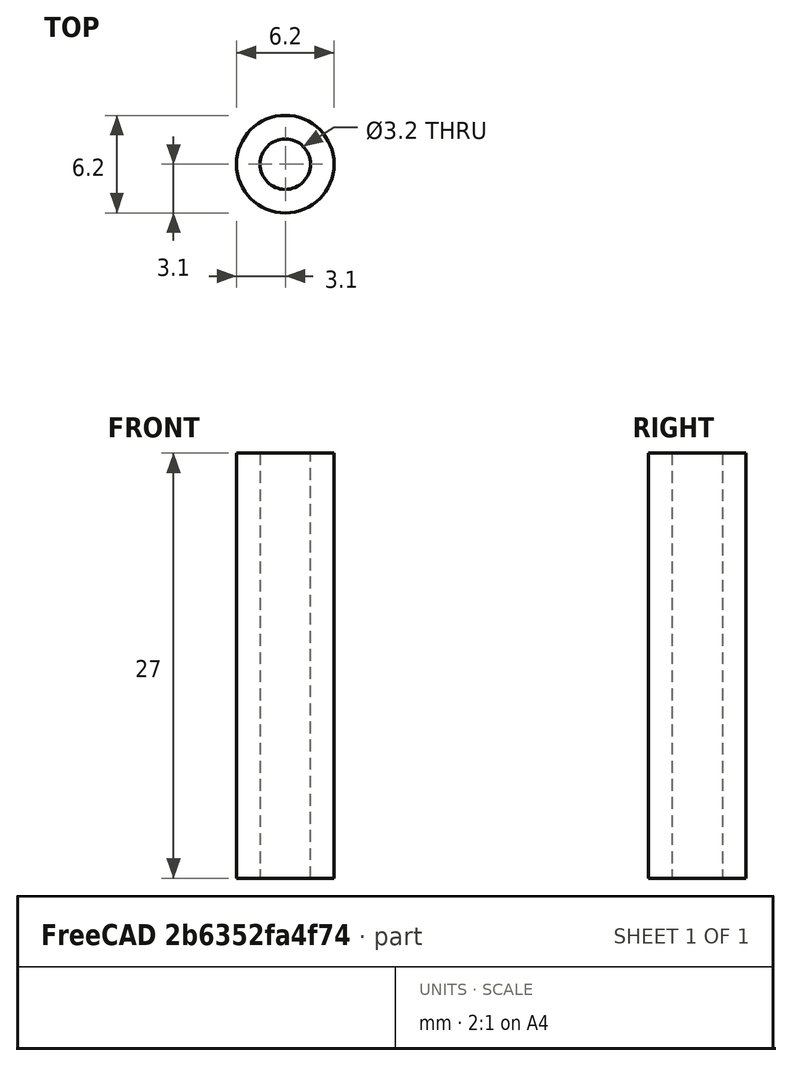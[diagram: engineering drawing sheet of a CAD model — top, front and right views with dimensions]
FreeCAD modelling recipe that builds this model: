
FCSTD DOCUMENT  (FreeCAD 0.20R29603 (Git))
Label: espacador-27mm
License: All rights reserved
LicenseURL: http://en.wikipedia.org/wiki/All_rights_reserved
objects: Sketcher::SketchObject×1, PartDesign::Pad×1, PartDesign::Body×1
note: 4 computed .brp shape members not serialized (recipe doc carries the construction recipe); baked Part::Feature solids carry a one-line shape summary decoded from their .brp

FEATURE [Sketcher::SketchObject] Sketch
  FullyConstrained = true
  MapMode = 5
  Support = -> [XY_Plane]
  sketch-geometry (4):
    g0: Circle CenterX=0 CenterY=0 CenterZ=0 NormalX=0 NormalY=0 NormalZ=1 AngleXU=0 Radius=3.1
    g1: Circle CenterX=0 CenterY=0 CenterZ=0 NormalX=0 NormalY=0 NormalZ=1 AngleXU=0 Radius=1.6
    g2: GeomPoint X=3.1 Y=0 Z=0
    g3: GeomPoint X=1.6 Y=0 Z=0
  constraints (9):
    c: Coincident(g0,g-1)
    c: Coincident(g1,g0)
    c: Radius(g1) = 1.6
    c: PointOnObject(g3,g1)
    c: PointOnObject(g3,g-1)
    c: PointOnObject(g2,g0)
    c: PointOnObject(g2,g-1)
    c: DistanceX(g3,g2) = 1.5
    c: Radius(g0) = 3.1
FEATURE [PartDesign::Pad] Pad
  Direction = (0,0,1)
  Length = 27
  Length2 = 10
  Profile = -> Sketch
  ReferenceAxis = -> Sketch [N_Axis]
  Type = 0
FEATURE [PartDesign::Body] Body
  Group = -> [Sketch,Pad]
  Origin = -> Origin
  Tip = -> Pad
